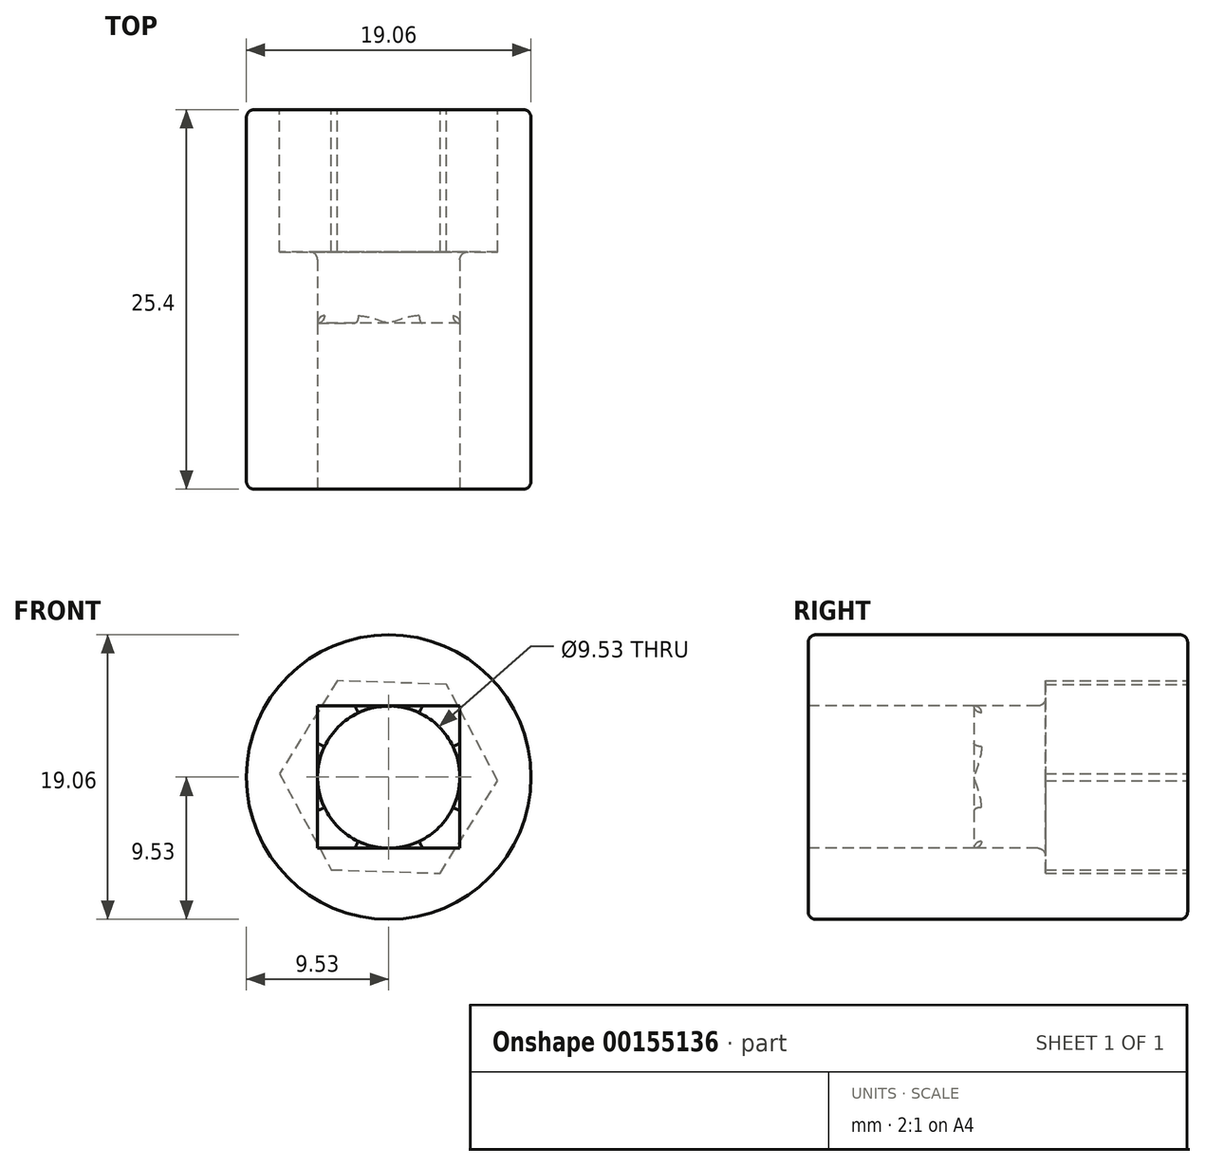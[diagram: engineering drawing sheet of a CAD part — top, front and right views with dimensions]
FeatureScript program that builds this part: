
annotation { "Feature Type Name" : "Feature", "Feature Type Description" : "" }
export const myFeature = defineFeature(function(context is Context, id is Id, definition is map)
    precondition{}
    {
        {
            var Q0;
            Q0=qCreatedBy(makeId("Front.planeOp"),FACE);
            var sketch = newSketch(context, id + "F0", { "sketchPlane" : qUnion([Q0])});
            skCircle(sketch, "E0", {"center": v(0, 0) * mm, "radius": 9.53 * mm});
            skSolve(sketch);
        }
        {
            var Q0;
            Q0 = qSketchRegion(id + "F0", true);
            extrude(context, id + "F1", {"entities" : qUnion([Q0]), "depth" : 25.4 * mm});
        }
        {
            var Q0;
            Q0=makeQuery(id+"F1.opExtrude","CAP_FACE",FACE,{"disambiguationData":[OSD([sQuery(id+"F0.wireOp",EDGE,"E0")])],"isStart":false});
            var sketch = newSketch(context, id + "F2", { "sketchPlane" : qUnion([Q0])});
            skLineSegment(sketch, "E1.bottom", {"start": v(4.76, 4.76) * mm, "end": v(-4.76, 4.76) * mm});
            skLineSegment(sketch, "E1.top", {"start": v(4.76, -4.76) * mm, "end": v(-4.76, -4.76) * mm});
            skLineSegment(sketch, "E1.left", {"start": v(4.76, 4.76) * mm, "end": v(4.76, -4.76) * mm});
            skLineSegment(sketch, "E1.right", {"start": v(-4.76, 4.76) * mm, "end": v(-4.76, -4.76) * mm});
            skPoint(sketch, "E1.middle", {"position": v(0, 0) * mm});
            skCircle(sketch, "E2", {"center": v(0, 0) * mm, "radius": 4.76 * mm});
            skSolve(sketch);
        }
        {
            var Q0;
            {var subQ0=sQuery(id+"F2.wireOp",EDGE,"E2");var subQ1=makeQuery(id+"F2.imprint","INTERSECT",VERTEX,{"derivedFrom":[sQuery(id+"F2.wireOp",EDGE,"E1.bottom"),subQ0]});Q0=makeQuery(id+"F2.imprint","IMPRINT",FACE,{"disambiguationData":[TD([[makeQuery(id+"F2.imprint","IMPRINT",EDGE,{"disambiguationData":[TD([[subQ1,1.0]])],"derivedFrom":subQ0}),1.0]])]});}
            extrude(context, id + "F3", {"entities" : qUnion([Q0]), "operationType" : NewBodyOperationType.REMOVE, "endBound" : BoundingType.THROUGH_ALL, "oppositeDirection" : true, "depth" : 25.4 * mm});
        }
        {
            var Q0;
            Q0 = qSketchRegion(id + "F2", true);
            extrude(context, id + "F4", {"entities" : qUnion([Q0]), "operationType" : NewBodyOperationType.REMOVE, "oppositeDirection" : true, "depth" : 11.1 * mm});
        }
        {
            var Q0;
            Q0=makeQuery(id+"F1.opExtrude","CAP_FACE",FACE,{"disambiguationData":[OSD([sQuery(id+"F0.wireOp",EDGE,"E0")])],"isStart":true});
            var sketch = newSketch(context, id + "F5", { "sketchPlane" : qUnion([Q0])});
            skCircle(sketch, "E3.cCircle", {"center": v(0, 0) * mm, "radius": 6.33 * mm, "construction": true});
            skLineSegment(sketch, "E3.0", {"start": v(3.44, 6.45) * mm, "end": v(7.3, 0.24) * mm});
            skLineSegment(sketch, "E3.1", {"start": v(7.3, 0.24) * mm, "end": v(3.86, -6.2) * mm});
            skLineSegment(sketch, "E3.2", {"start": v(3.86, -6.2) * mm, "end": v(-3.44, -6.45) * mm});
            skLineSegment(sketch, "E3.3", {"start": v(-3.44, -6.45) * mm, "end": v(-7.3, -0.24) * mm});
            skLineSegment(sketch, "E3.4", {"start": v(-7.3, -0.24) * mm, "end": v(-3.86, 6.2) * mm});
            skLineSegment(sketch, "E3.5", {"start": v(-3.86, 6.2) * mm, "end": v(3.44, 6.45) * mm});
            skPoint(sketch, "E3.0.midPoint", {"position": v(5.37, 3.34) * mm});
            skSolve(sketch);
        }
        {
            var Q0;
            Q0 = qSketchRegion(id + "F5", true);
            extrude(context, id + "F6", {"entities" : qUnion([Q0]), "operationType" : NewBodyOperationType.REMOVE, "oppositeDirection" : true, "depth" : 9.52 * mm});
        }
        {
            var Q0;
            Q0=makeQuery(id+"F1.opExtrude","CAP_EDGE",EDGE,{"disambiguationData":[OSD([sQuery(id+"F0.wireOp",EDGE,"E0")])],"isStart":true});
            var Q1;
            Q1=makeQuery(id+"F1.opExtrude","CAP_EDGE",EDGE,{"disambiguationData":[OSD([sQuery(id+"F0.wireOp",EDGE,"E0")])],"isStart":false});
            var Q2;
            Q2=makeQuery(id+"F4.boolean.opBoolean","COPY",EDGE,{"derivedFrom":makeQuery(id+"F4.opExtrude","CAP_EDGE",EDGE,{"disambiguationData":[OSD([sQuery(id+"F2.wireOp",EDGE,"E1.bottom")])],"isStart":true})});
            var Q3;
            Q3=makeQuery(id+"F4.boolean.opBoolean","COPY",EDGE,{"derivedFrom":makeQuery(id+"F4.opExtrude","CAP_EDGE",EDGE,{"disambiguationData":[OSD([sQuery(id+"F2.wireOp",EDGE,"E1.right")])],"isStart":true})});
            var Q4;
            Q4=makeQuery(id+"F4.boolean.opBoolean","COPY",EDGE,{"derivedFrom":makeQuery(id+"F4.opExtrude","CAP_EDGE",EDGE,{"disambiguationData":[OSD([sQuery(id+"F2.wireOp",EDGE,"E1.left")])],"isStart":true})});
            var Q5;
            Q5=makeQuery(id+"F4.boolean.opBoolean","COPY",EDGE,{"derivedFrom":makeQuery(id+"F4.opExtrude","CAP_EDGE",EDGE,{"disambiguationData":[OSD([sQuery(id+"F2.wireOp",EDGE,"E1.top")])],"isStart":true})});
            var Q6;
            Q6=makeQuery(id+"F4.boolean.opBoolean","INTERSECT",EDGE,{"disambiguationData":[OD(1.0)],"derivedFrom":[makeQuery(id+"F3.boolean.opBoolean","COPY",FACE,{"derivedFrom":makeQuery(id+"F3.opExtrude","SWEPT_FACE",FACE,{"disambiguationData":[OSD([sQuery(id+"F2.wireOp",EDGE,"E2")])]})}),makeQuery(id+"F4.opExtrude","CAP_FACE",FACE,{"disambiguationData":[OSD([sQuery(id+"F2.wireOp",EDGE,"E1.bottom"),sQuery(id+"F2.wireOp",EDGE,"E1.top"),sQuery(id+"F2.wireOp",EDGE,"E1.left"),sQuery(id+"F2.wireOp",EDGE,"E1.right")])],"isStart":false})]});
            var Q7;
            Q7=makeQuery(id+"F6.boolean.opBoolean","INTERSECT",EDGE,{"derivedFrom":[makeQuery(id+"F3.boolean.opBoolean","COPY",FACE,{"derivedFrom":makeQuery(id+"F3.opExtrude","SWEPT_FACE",FACE,{"disambiguationData":[OSD([sQuery(id+"F2.wireOp",EDGE,"E2")])]})}),makeQuery(id+"F6.opExtrude","CAP_FACE",FACE,{"disambiguationData":[OSD([sQuery(id+"F5.wireOp",EDGE,"E3.0"),sQuery(id+"F5.wireOp",EDGE,"E3.1"),sQuery(id+"F5.wireOp",EDGE,"E3.2"),sQuery(id+"F5.wireOp",EDGE,"E3.3"),sQuery(id+"F5.wireOp",EDGE,"E3.4"),sQuery(id+"F5.wireOp",EDGE,"E3.5")])],"isStart":false})]});
            var Q8;
            Q8=makeQuery(id+"F6.boolean.opBoolean","COPY",EDGE,{"derivedFrom":makeQuery(id+"F6.opExtrude","CAP_EDGE",EDGE,{"disambiguationData":[OSD([sQuery(id+"F5.wireOp",EDGE,"E3.4")])],"isStart":true})});
            var Q9;
            Q9=makeQuery(id+"F6.boolean.opBoolean","COPY",EDGE,{"derivedFrom":makeQuery(id+"F6.opExtrude","CAP_EDGE",EDGE,{"disambiguationData":[OSD([sQuery(id+"F5.wireOp",EDGE,"E3.5")])],"isStart":true})});
            var Q10;
            Q10=makeQuery(id+"F6.boolean.opBoolean","COPY",EDGE,{"derivedFrom":makeQuery(id+"F6.opExtrude","CAP_EDGE",EDGE,{"disambiguationData":[OSD([sQuery(id+"F5.wireOp",EDGE,"E3.0")])],"isStart":true})});
            var Q11;
            Q11=makeQuery(id+"F6.boolean.opBoolean","COPY",EDGE,{"derivedFrom":makeQuery(id+"F6.opExtrude","CAP_EDGE",EDGE,{"disambiguationData":[OSD([sQuery(id+"F5.wireOp",EDGE,"E3.1")])],"isStart":true})});
            var Q12;
            Q12=makeQuery(id+"F6.boolean.opBoolean","COPY",EDGE,{"derivedFrom":makeQuery(id+"F6.opExtrude","CAP_EDGE",EDGE,{"disambiguationData":[OSD([sQuery(id+"F5.wireOp",EDGE,"E3.2")])],"isStart":true})});
            var Q13;
            Q13=makeQuery(id+"F6.boolean.opBoolean","COPY",EDGE,{"derivedFrom":makeQuery(id+"F6.opExtrude","CAP_EDGE",EDGE,{"disambiguationData":[OSD([sQuery(id+"F5.wireOp",EDGE,"E3.3")])],"isStart":true})});
            fillet(context, id + "F7", {"entities" : qUnion([Q0, Q1, Q2, Q3, Q4, Q5, Q6, Q7, Q8, Q9, Q10, Q11, Q12, Q13]), "radius" : 0.5 * mm, "tangentPropagation" : true, "allowEdgeOverflow" : false});
        }
    });
